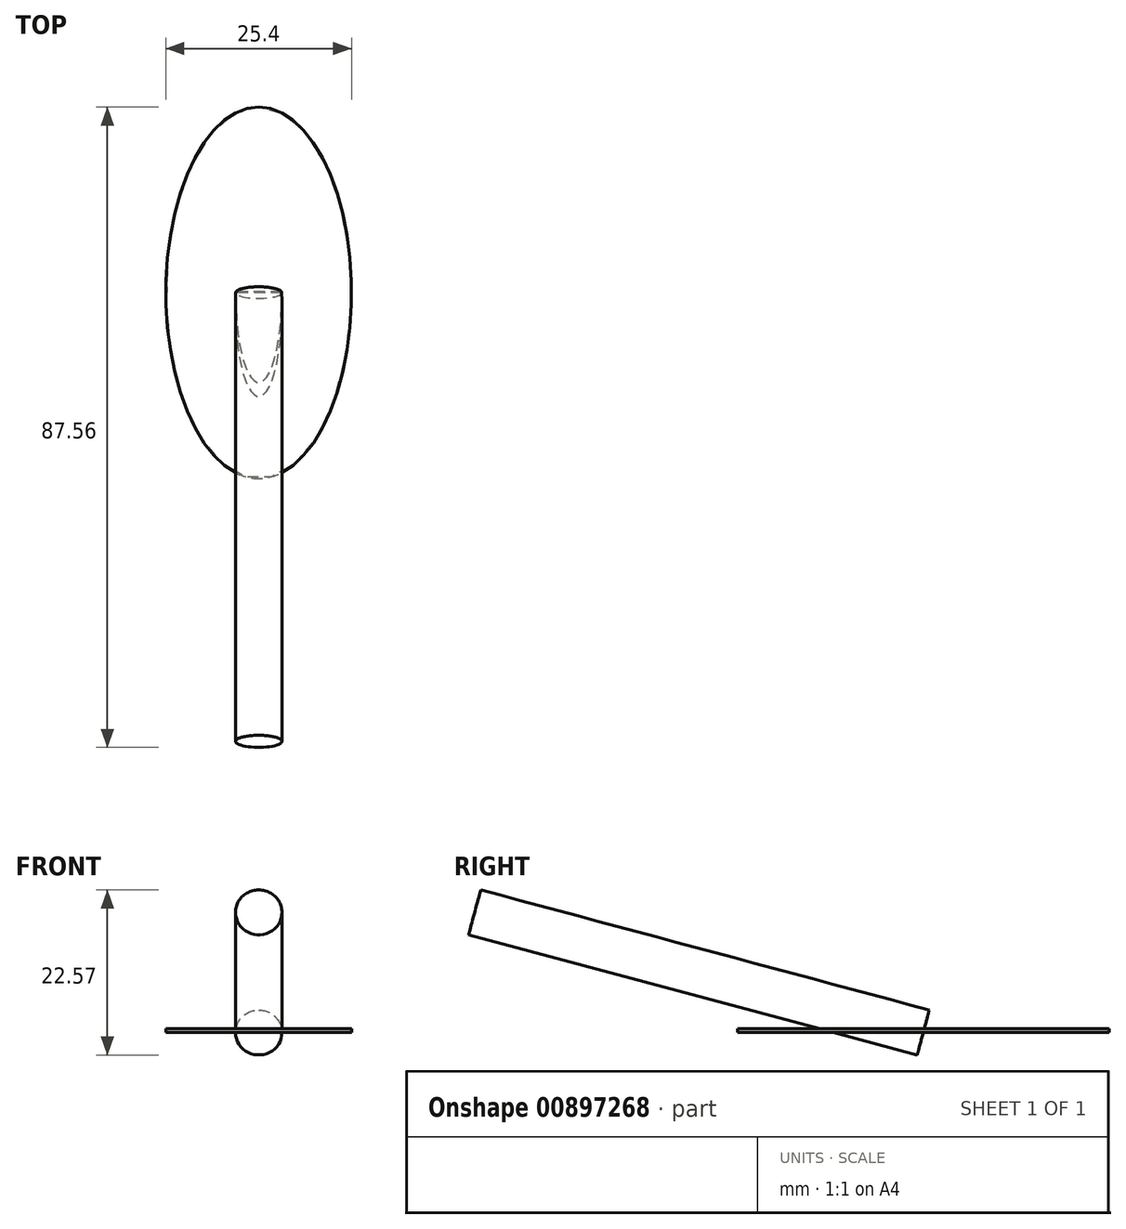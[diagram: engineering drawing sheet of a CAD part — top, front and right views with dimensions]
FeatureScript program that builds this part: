
annotation { "Feature Type Name" : "Feature", "Feature Type Description" : "" }
export const myFeature = defineFeature(function(context is Context, id is Id, definition is map)
    precondition{}
    {
        {
            var Q0;
            Q0=qCreatedBy(makeId("Top.planeOp"),FACE);
            var sketch = newSketch(context, id + "F0", { "sketchPlane" : qUnion([Q0])});
            skEllipse(sketch, "E0", {"center": v(0, 0) * mm, "majorRadius": 25.4 * mm, "minorRadius": 12.7 * mm, "majorAxis": v(0, 1)});
            skLineSegment(sketch, "E1", {"start": v(-12.7, 0) * mm, "end": v(12.7, 0) * mm, "construction": true});
            skSolve(sketch);
        }
        {
            var Q0;
            Q0=makeQuery(id+"F0.imprint","IMPRINT",FACE,{"disambiguationData":[TD([[makeQuery(id+"F0.imprint","IMPRINT",EDGE,{"derivedFrom":sQuery(id+"F0.wireOp",EDGE,"E0")}),1.0]])]});
            extrude(context, id + "F1", {"entities" : qUnion([Q0]), "depth" : 0.5 * mm, "offsetDistance" : 25.4 * mm});
        }
        {
            var Q0;
            Q0=sQuery(id+"F0.wireOp",EDGE,"E1");
            cPlane(context, id + "F2", {"entities" : qUnion([Q0]), "cplaneType" : CPlaneType.LINE_ANGLE, "offset" : 25.4 * mm, "angle" : 15 * degree, "oppositeDirection" : true, "width" : 152.4 * mm, "height" : 152.4 * mm});
        }
        {
            var Q0;
            Q0=qCreatedBy(id+"F2.planeOp",FACE);
            var sketch = newSketch(context, id + "F3", { "sketchPlane" : qUnion([Q0])});
            skCircle(sketch, "E2", {"center": v(0, 0) * mm, "radius": 3.18 * mm});
            skSolve(sketch);
        }
        {
            var Q0;
            Q0=makeQuery(id+"F3.imprint","IMPRINT",FACE,{"disambiguationData":[TD([[makeQuery(id+"F3.imprint","IMPRINT",EDGE,{"derivedFrom":sQuery(id+"F3.wireOp",EDGE,"E2")}),1.0]])]});
            extrude(context, id + "F4", {"entities" : qUnion([Q0]), "operationType" : NewBodyOperationType.ADD, "oppositeDirection" : true, "depth" : 63.5 * mm, "offsetDistance" : 25.4 * mm});
        }
    });
